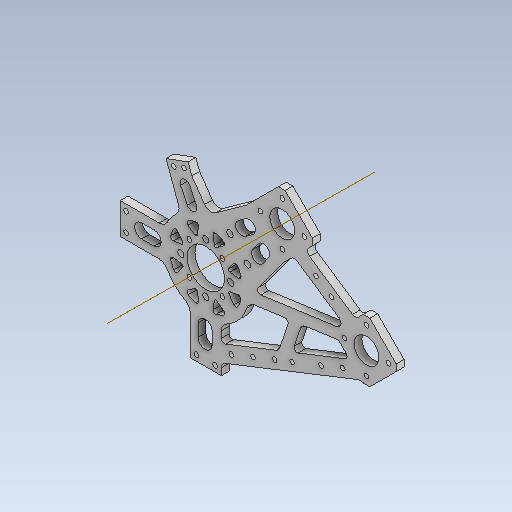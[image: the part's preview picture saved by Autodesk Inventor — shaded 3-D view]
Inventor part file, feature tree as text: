
AUTODESK INVENTOR PART (.ipt)
format: ipt  version: 2020 (Build 240168000, 168)  size: 1,525,760 bytes
history: native  units: mm
features: sketch x19, extrude x15, reference x14, projected_geometry x14, other x11, fillet x9, thicken_offset x5, hole x4, chamfer x1, plane x1, mirror x1
ambient origin geometry x8: Origin, YZ Plane, XZ Plane, XY Plane, X Axis, Y Axis, Z Axis, Center Point
bodies: Solid1 (feature_tree)
feature tree (94):
  extrude  "Extrusion1"  Depth=68.5mm
  extrude  "Extrusion2"  Depth=30.0mm
  extrude  "Extrusion3"  Depth=5.0mm TaperAngle=0.0deg
  thicken_offset  "Thicken1"
  thicken_offset  "Thicken2"
  thicken_offset  "Thicken3"
  sketch  "Sketch5"  dims[d7=69.5mm d8=16.0mm]
  extrude  "Extrusion6"  Depth=16.0mm
  extrude  "Extrusion7"  Depth=33.0mm
  hole  "Hole2"  [1 undecoded]
  hole  "Hole4"  [1 undecoded]
  fillet  "Fillet1"  Radius=33.0mm
  extrude  "Extrusion11"  Depth=2.0mm
  thicken_offset  "Thicken4"
  hole  "Hole6"  [1 undecoded]
  extrude  "Extrusion12"  Depth=2.0mm
  extrude  "Extrusion16"  Depth=2.0mm
  extrude  "Extrusion17"  Depth=10.0mm TaperAngle=0.0deg
  extrude  "Extrusion18"  Depth=15.0mm
  chamfer  "Chamfer2"  Distance=1.0mm
  fillet  "Fillet3"  Radius=3.0mm
  fillet  "Fillet4"  Radius=8.0mm
  fillet  "Fillet5"  Radius=1.0mm
  fillet  "Fillet6"  Radius=3.0mm
  extrude  "Extrusion19"  Depth=8.0mm
  plane  "Work Plane2"
  mirror  "Mirror2"
  extrude  "Extrusion20"  Depth=5.0mm TaperAngle=0.0deg
  fillet  "Fillet7"  Radius=1.0mm
  fillet  "Fillet8"  Radius=1.0mm
  hole  "Hole7"  [1 undecoded]
  extrude  "Extrusion21"  Depth=20.0mm
  fillet  "Fillet9"  Radius=10.0mm
  fillet  "Fillet10"  Radius=10.0mm
  extrude  "Extrusion22"  Depth=45.0mm
  extrude  "Extrusion23"  Depth=7.0mm
  thicken_offset  "Thicken5"
  sketch  "Sketch1"  dims[d0=60.0mm d1=68.5mm]
  reference  "Reference1"
  sketch  "Sketch2"  dims[d2=35.0mm d3=30.0mm]
  projected_geometry  "Projected Loop1"
  sketch  "Sketch3"  dims[d4=52.0mm d5=5.0mm d6=0.0mm]
  projected_geometry  "Projected Loop2"
  sketch  "Sketch7"  dims[d9=5.0mm d10=0.0mm d11=33.0mm]
  reference  "Reference4"
  reference  "Reference5"
  projected_geometry  "Projected Loop5"
  sketch  "Sketch10"  dims[d12=33.0mm d13=20.0mm]
  reference  "Reference7"
  reference  "Reference8"
  reference  "Reference9"
  reference  "Reference10"
  sketch  "Sketch13"  dims[d14=33.0mm d15=20.0mm d16=33.0mm]
  projected_geometry  "Projected Loop8"
  sketch  "Sketch16"  dims[d17=5.0mm d18=0.0mm d19=2.0mm]
  projected_geometry  "Projected Loop11"
  sketch  "Sketch17"  dims[d20=2.0mm d21=2.0mm]
  projected_geometry  "Projected Loop12"
  sketch  "Sketch18"  dims[d22=2.0mm d23=2.0mm]
  reference  "Reference11"
  projected_geometry  "Projected Loop13"
  sketch  "Sketch23"  dims[d24=2.0mm d46=56.0mm]
  reference  "Reference14"
  projected_geometry  "Projected Loop17"
  sketch  "Sketch24"  dims[d47=5.0mm d48=0.0mm d49=10.0mm d50=0.0mm]
  reference  "Reference15"
  reference  "Reference16"
  sketch  "Sketch25"  dims[d53=3.0mm d54=6.0mm d55=4.0mm d56=2.0mm d57=90.0deg d58=7.0mm d59=0.0mm d75=15.0mm]
  reference  "Reference17"
  reference  "Reference18"
  sketch  "Sketch26"  dims[d76=8.0mm]
  projected_geometry  "Projected Loop18"
  sketch  "Sketch27"  dims[d78=8.0mm]
  projected_geometry  "Projected Loop19"
  sketch  "Sketch28"  dims[d79=4.15mm d80=6.0mm d81=4.0mm d82=2.0mm d83=90.0deg d84=7.0mm d85=0.0mm]
  projected_geometry  "Projected Loop20"
  sketch  "Sketch29"  dims[d94=6.0mm]
  reference  "Reference19"
  projected_geometry  "Projected Loop21"
  sketch  "Sketch30"  dims[d103=13.0mm]
  projected_geometry  "Projected Loop22"
  sketch  "Sketch31"  dims[d104=13.0mm d105=1.0mm d106=3.0mm d107=8.0mm d108=1.0mm d109=3.0mm d110=8.0mm d111=5.0mm d112=0.0mm d116=1.0mm d117=1.0mm d118=20.0mm d119=20.0mm d120=3.0mm d121=6.0mm d122=4.0mm d123=2.0mm d124=90.0deg d125=17.0mm d126=0.0mm d127=10.0mm d128=0.0mm d149=10.0mm d150=45.0mm d151=7.0mm d152=65.0mm d153=10.0mm d154=10.0mm d155=100.0mm d156=5.0mm d157=0.0mm d158=3.0mm d159=3.0mm d160=5.0mm d161=0.0mm d162=10.0mm d163=0.0mm d164=3.0mm d165=2.0mm d166=45.0deg d167=4.0mm d168=3.0mm d169=2.0mm d170=6.0mm d171=14.0mm d172=4.0mm d173=9.0mm d174=10.0mm d175=0.0mm d176=7.0mm d177=30.0mm d178=5.0mm d179=0.0mm d180=2.0mm d181=4.0mm d182=15.0mm d183=15.0mm d184=20.0mm d185=15.0mm d186=3.0mm d187=6.0mm d188=4.0mm d189=2.0mm d190=90.0deg d191=17.0mm d192=0.0mm d193=5.0mm d194=10.0mm d195=0.0mm d196=5.0mm d197=5.0mm d198=4.0mm d199=4.0mm d200=3.0mm d201=3.0mm d202=10.0mm d203=0.0mm d204=14.0mm d205=20.245819mm d206=5.0mm d207=7.5mm d208=10.0mm d209=0.0mm d210=0.5mm d211=0.5mm d138=0.5mm d139=0.872665mm d140=0.5mm d141=0.872665mm]
  projected_geometry  "Projected Loop23"
  parser-record x2  (decoder bookkeeping rows leaked as tree rows — omitted from the tree; the rows remain in map.json)
  other  "reducer_1.iam"
  other  "90_motor:1"
  other  "90motor_base:1"
  other  "motor_holder_3:1"
  other  "motor_holder_2:1"
  other  "motor_holder_5:1"
  other  "slide_holder_1:1"
  other  "slide_holder_2:1"
  other  "motor_holder_6:1"
note: 4 required parameter values undecoded (feature->parameter linkage not recoverable at this tier; creation-order binding heuristic only, values carry confidence <= 0.55)
note: 2 file-system paths scrubbed to <path> (originals preserved in map.json)
